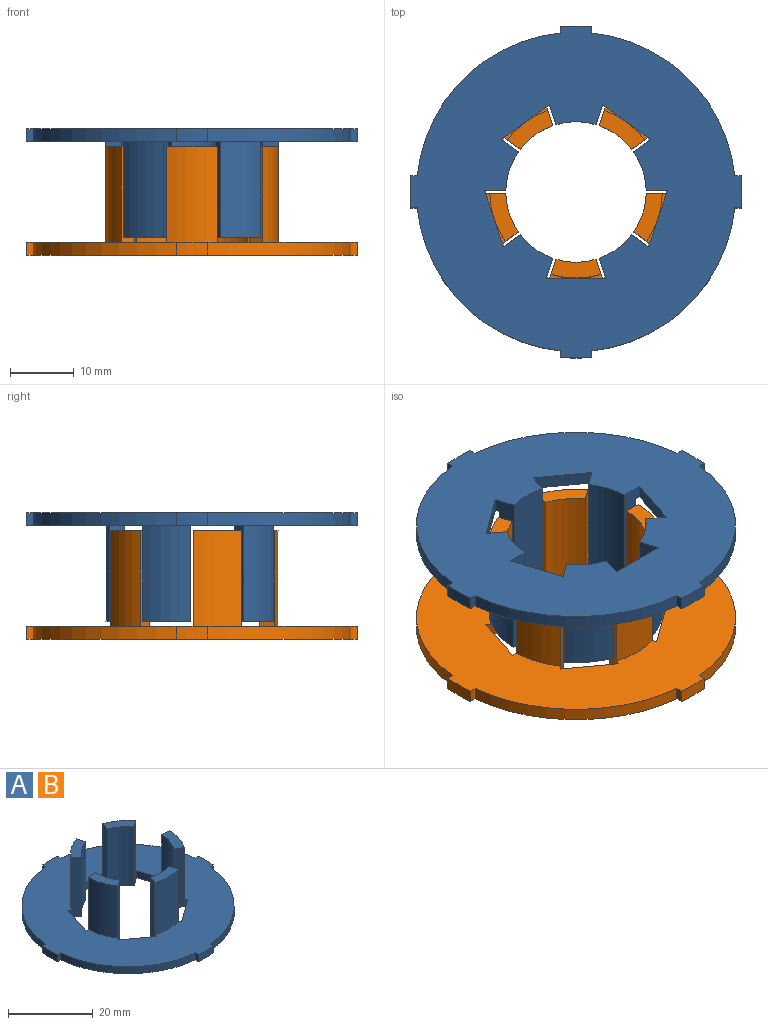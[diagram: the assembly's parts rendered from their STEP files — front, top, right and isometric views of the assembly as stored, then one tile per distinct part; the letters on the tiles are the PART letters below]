
ASSEMBLY  parts=2 mates=1
PART A: 48 faces, bbox 52x52x17 mm
  f0: plane 52x52mm, normal (0,0,1), area 1398.2mm2, adj f2,f3,f4,f5,f8,f11,f14,f17
  f1: plane 52x52mm, normal (0,0,-1), area 1488.1mm2, adj f2,f3,f4,f7,f10,f13,f16,f19
  f2: cylinder r=26mm len=5mm, axis (0,0,-1), area 10mm2, adj f0,f1,f42,f46
  f3: cylinder r=26mm len=5mm, axis (0,0,-1), area 10mm2, adj f0,f1,f39,f43
  f4: cylinder r=26mm len=5mm, axis (0,0,-1), area 10mm2, adj f0,f1,f38,f40
  f5: cylinder r=13.5mm len=15mm, axis (0,0,-1), area 119.6mm2, adj f0,f6,f32,f34
  f6: plane 7.48x4.45mm, normal (0,0,1), area 18mm2, adj f5,f7,f32,f34
  f7: cylinder r=11mm len=17mm, axis (0,0,1), area 108.8mm2, adj f1,f6,f32,f34
  f8: cylinder r=13.5mm len=15mm, axis (0,0,-1), area 119.6mm2, adj f0,f9,f29,f31
  f9: plane 7.86x2.96mm, normal (0,0,1), area 18mm2, adj f8,f10,f29,f31
  f10: cylinder r=11mm len=17mm, axis (0,0,1), area 108.8mm2, adj f1,f9,f29,f31
  f11: cylinder r=13.5mm len=15mm, axis (0,0,-1), area 119.6mm2, adj f0,f12,f26,f28
  f12: plane 7.48x4.45mm, normal (0,0,1), area 18mm2, adj f11,f13,f26,f28
  f13: cylinder r=11mm len=17mm, axis (0,0,1), area 108.8mm2, adj f1,f12,f26,f28
  f14: cylinder r=13.5mm len=15mm, axis (0,0,-1), area 119.6mm2, adj f0,f15,f23,f25
  f15: plane 7.13x6.09mm, normal (0,0,1), area 18mm2, adj f14,f16,f23,f25
  f16: cylinder r=11mm len=17mm, axis (0,0,1), area 108.8mm2, adj f1,f15,f23,f25
  f17: cylinder r=13.5mm len=15mm, axis (0,0,-1), area 119.6mm2, adj f0,f18,f22,f35
  f18: plane 7.13x6.09mm, normal (0,0,1), area 18mm2, adj f17,f20,f22,f35
  f19: cylinder r=26mm len=5mm, axis (0,0,-1), area 10mm2, adj f0,f1,f36,f45
  f20: cylinder r=11mm len=17mm, axis (0,0,1), area 108.8mm2, adj f1,f18,f22,f35
  f21: plane 9.32x2mm, normal (0,-1,0), area 18.6mm2, adj f0,f1,f22,f23
  f22: plane 17x3.14mm, normal (-0.95,0.31,0), area 44.1mm2, adj f0,f1,f17,f18,f20,f21
  f23: plane 17x3.14mm, normal (0.95,0.31,0), area 44.1mm2, adj f0,f1,f14,f15,f16,f21
  f24: plane 8.86x2.88mm, normal (0.95,-0.31,0), area 18.6mm2, adj f0,f1,f25,f26
  f25: plane 17x2.67mm, normal (-0.59,-0.81,0), area 44.1mm2, adj f0,f1,f14,f15,f16,f24
  f26: plane 17x3.3mm, normal (0,1,0), area 44.1mm2, adj f0,f1,f11,f12,f13,f24
  f27: plane 7.54x5.48mm, normal (0.59,0.81,0), area 18.6mm2, adj f0,f1,f28,f29
  f28: plane 17x2.67mm, normal (0.59,-0.81,0), area 44.1mm2, adj f0,f1,f11,f12,f13,f27
  f29: plane 17x3.14mm, normal (-0.95,0.31,0), area 44.1mm2, adj f0,f1,f8,f9,f10,f27
  f30: plane 7.54x5.48mm, normal (-0.59,0.81,0), area 18.6mm2, adj f0,f1,f31,f32
  f31: plane 17x3.14mm, normal (0.95,0.31,0), area 44.1mm2, adj f0,f1,f8,f9,f10,f30
  f32: plane 17x2.67mm, normal (-0.59,-0.81,0), area 44.1mm2, adj f0,f1,f5,f6,f7,f30
  f33: plane 8.86x2.88mm, normal (-0.95,-0.31,0), area 18.6mm2, adj f0,f1,f34,f35
  f34: plane 17x3.3mm, normal (0,1,0), area 44.1mm2, adj f0,f1,f5,f6,f7,f33
  f35: plane 17x2.67mm, normal (0.59,-0.81,0), area 44.1mm2, adj f0,f1,f17,f18,f20,f33
  f36: plane 2x1.01mm, normal (1,0,0), area 2mm2, adj f0,f1,f19,f37
  f37: cylinder r=25mm len=22.37mm, axis (0,0,1), area 68.5mm2, adj f0,f1,f36,f38
  f38: plane 2x1.01mm, normal (0,1,0), area 2mm2, adj f0,f1,f4,f37
  f39: plane 2x1.01mm, normal (1,0,0), area 2mm2, adj f0,f1,f3,f41
  f40: plane 2x1.01mm, normal (0,-1,0), area 2mm2, adj f0,f1,f4,f41
  f41: cylinder r=25mm len=22.37mm, axis (0,0,1), area 68.5mm2, adj f0,f1,f39,f40
  f42: plane 2x1.01mm, normal (0,-1,0), area 2mm2, adj f0,f1,f2,f44
  f43: plane 2x1.01mm, normal (-1,0,0), area 2mm2, adj f0,f1,f3,f44
  f44: cylinder r=25mm len=22.37mm, axis (0,0,1), area 68.5mm2, adj f0,f1,f42,f43
  f45: plane 2x1.01mm, normal (-1,0,0), area 2mm2, adj f0,f1,f19,f47
  f46: plane 2x1.01mm, normal (0,1,0), area 2mm2, adj f0,f1,f2,f47
  f47: cylinder r=25mm len=22.37mm, axis (0,0,1), area 68.5mm2, adj f0,f1,f45,f46
PART B: same geometry as A
PLACE A rot(axis=(1,0,0),180deg) t=(-1.18,-1.17,30.51)mm
PLACE B t=(-1.18,-1.17,10.71)mm
MATE cylindrical A.f7 <-> B.f7  axis (0,0,-1) through (-1.18,-1.17,13.51)mm
